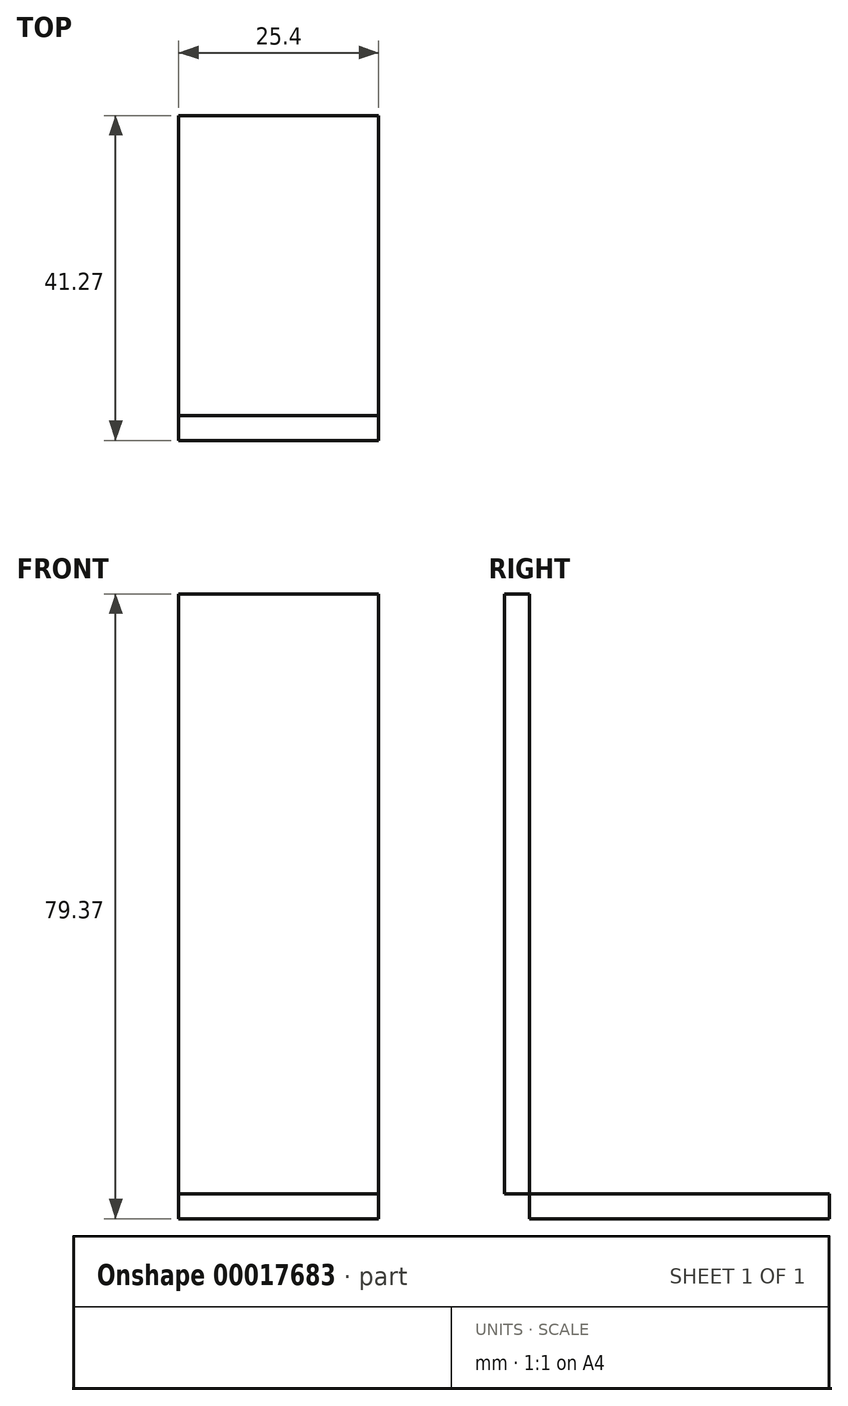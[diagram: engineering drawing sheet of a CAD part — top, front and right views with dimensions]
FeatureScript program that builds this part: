
annotation { "Feature Type Name" : "Feature", "Feature Type Description" : "" }
export const myFeature = defineFeature(function(context is Context, id is Id, definition is map)
    precondition{}
    {
        {
            var Q0;
            Q0=qCreatedBy(makeId("Front.planeOp"),FACE);
            var sketch = newSketch(context, id + "F0", { "sketchPlane" : qUnion([Q0])});
            skLineSegment(sketch, "E0.bottom", {"start": v(0, 0) * mm, "end": v(25.4, 0) * mm});
            skLineSegment(sketch, "E0.top", {"start": v(0, 76.2) * mm, "end": v(25.4, 76.2) * mm});
            skLineSegment(sketch, "E0.left", {"start": v(0, 0) * mm, "end": v(0, 76.2) * mm});
            skLineSegment(sketch, "E0.right", {"start": v(25.4, 0) * mm, "end": v(25.4, 76.2) * mm});
            skSolve(sketch);
        }
        {
            var Q0;
            Q0=makeQuery(id+"F0.imprint","IMPRINT",FACE,{"disambiguationData":[TD([[makeQuery(id+"F0.imprint","IMPRINT",EDGE,{"derivedFrom":sQuery(id+"F0.wireOp",EDGE,"E0.bottom")}),1.0]])]});
            extrude(context, id + "F1", {"entities" : qUnion([Q0]), "depth" : 3.17 * mm});
        }
        {
            var Q0;
            Q0=qCreatedBy(makeId("Top.planeOp"),FACE);
            var sketch = newSketch(context, id + "F2", { "sketchPlane" : qUnion([Q0])});
            skLineSegment(sketch, "E1.bottom", {"start": v(0, 0) * mm, "end": v(25.4, 0) * mm});
            skLineSegment(sketch, "E1.top", {"start": v(0, 38.1) * mm, "end": v(25.4, 38.1) * mm});
            skLineSegment(sketch, "E1.left", {"start": v(0, 0) * mm, "end": v(0, 38.1) * mm});
            skLineSegment(sketch, "E1.right", {"start": v(25.4, 0) * mm, "end": v(25.4, 38.1) * mm});
            skSolve(sketch);
        }
        {
            var Q0;
            Q0=makeQuery(id+"F2.imprint","IMPRINT",FACE,{"disambiguationData":[TD([[makeQuery(id+"F2.imprint","IMPRINT",EDGE,{"derivedFrom":sQuery(id+"F2.wireOp",EDGE,"E1.bottom")}),1.0]])]});
            extrude(context, id + "F3", {"entities" : qUnion([Q0]), "operationType" : NewBodyOperationType.ADD, "oppositeDirection" : true, "depth" : 3.17 * mm});
        }
    });
